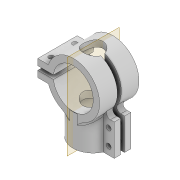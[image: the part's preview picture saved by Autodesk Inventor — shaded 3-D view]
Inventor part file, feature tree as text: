
AUTODESK INVENTOR PART (.ipt)
format: ipt  version: 2022 (Build 260153000, 153)  size: 331,776 bytes
history: native  units: mm
features: extrude x5, sketch x4, fillet x1
ambient origin geometry x8: Origin, YZ Plane, XZ Plane, XY Plane, X Axis, Y Axis, Z Axis, Center Point
bodies: Solid1 (feature_tree)
feature tree (10):
  sketch  "Sketch1"  dims[d0=35.0mm d1=8.0mm]
  extrude  "Extrusion1"  Depth=8.0mm
  extrude  "Extrusion4"  Depth=8.0mm
  extrude  "Extrusion5"  Depth=2.5mm
  fillet  "Fillet1"  Radius=20.0mm
  extrude  "Extrusion6"  Depth=10.0mm TaperAngle=0.0deg
  extrude  "Extrusion7"  Depth=10.0mm
  sketch  "Sketch4"  dims[d2=8.0mm d3=8.0mm]
  sketch  "Sketch5"  dims[d7=2.5mm d8=2.5mm d9=20.0mm]
  sketch  "Sketch6"  dims[d10=20.0mm d11=40.0mm d12=0.0mm d24=50.5mm d25=8.0mm d26=8.0mm d27=8.0mm d28=20.0mm d29=20.0mm d30=2.5mm d31=50.0mm d32=0.0mm d33=100.0mm d34=0.0mm d35=25.0mm d36=5.0mm d37=6.2mm d38=6.2mm d39=10.0mm d40=10.0mm d41=7.0mm d42=7.0mm d43=100.0mm d44=0.0mm d45=6.2mm d46=6.2mm d47=7.0mm d48=7.0mm d49=10.0mm d50=10.0mm d51=100.0mm d52=0.0mm]
